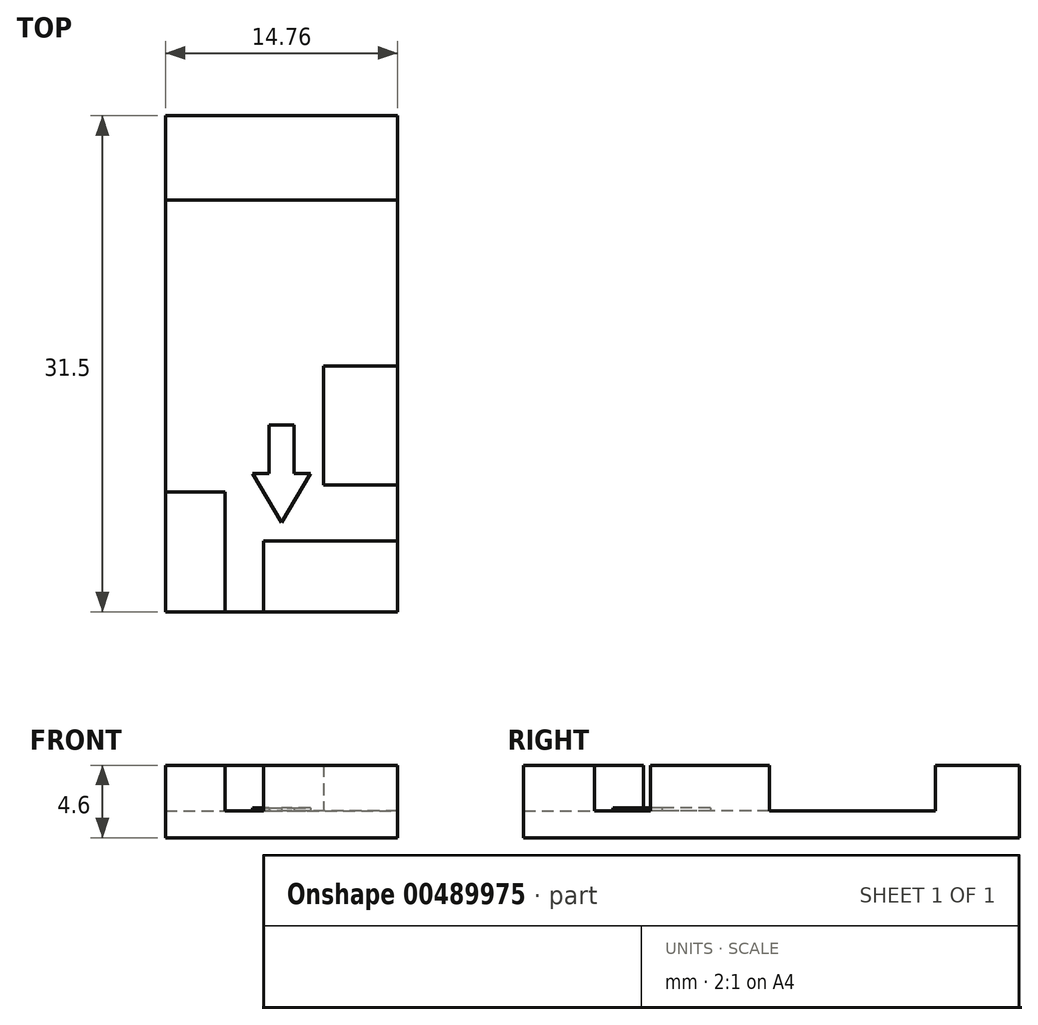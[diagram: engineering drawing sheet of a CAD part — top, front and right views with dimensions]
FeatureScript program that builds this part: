
annotation { "Feature Type Name" : "Feature", "Feature Type Description" : "" }
export const myFeature = defineFeature(function(context is Context, id is Id, definition is map)
    precondition{}
    {
        {
            var Q0;
            Q0=qCreatedBy(makeId("Top.planeOp"),FACE);
            var sketch = newSketch(context, id + "F0", { "sketchPlane" : qUnion([Q0])});
            skLineSegment(sketch, "E0.bottom", {"start": v(7.38, -15.75) * mm, "end": v(-7.38, -15.75) * mm});
            skLineSegment(sketch, "E0.top", {"start": v(7.38, 15.75) * mm, "end": v(-7.37, 15.75) * mm});
            skLineSegment(sketch, "E0.left", {"start": v(7.38, -15.75) * mm, "end": v(7.38, 15.75) * mm});
            skLineSegment(sketch, "E0.right", {"start": v(-7.38, -15.75) * mm, "end": v(-7.37, 15.75) * mm});
            skPoint(sketch, "E0.middle", {"position": v(0, 0) * mm});
            skSolve(sketch);
        }
        {
            var Q0;
            Q0=makeQuery(id+"F0.imprint","IMPRINT",FACE,{"disambiguationData":[TD([[makeQuery(id+"F0.imprint","IMPRINT",EDGE,{"derivedFrom":sQuery(id+"F0.wireOp",EDGE,"E0.bottom")}),-1.0]])]});
            extrude(context, id + "F1", {"entities" : qUnion([Q0]), "depth" : 1.7 * mm});
        }
        {
            var Q0;
            Q0=makeQuery(id+"F1.opExtrude","CAP_FACE",FACE,{"disambiguationData":[OSD([sQuery(id+"F0.wireOp",EDGE,"E0.bottom"),sQuery(id+"F0.wireOp",EDGE,"E0.top"),sQuery(id+"F0.wireOp",EDGE,"E0.left"),sQuery(id+"F0.wireOp",EDGE,"E0.right")])],"isStart":false});
            var sketch = newSketch(context, id + "F2", { "sketchPlane" : qUnion([Q0])});
            skLineSegment(sketch, "E1.bottom", {"start": v(-7.37, 15.75) * mm, "end": v(7.38, 15.75) * mm});
            skLineSegment(sketch, "E1.top", {"start": v(-7.37, 10.4) * mm, "end": v(7.38, 10.4) * mm});
            skLineSegment(sketch, "E1.left", {"start": v(-7.37, 15.75) * mm, "end": v(-7.37, 10.4) * mm});
            skLineSegment(sketch, "E1.right", {"start": v(7.38, 15.75) * mm, "end": v(7.38, 10.4) * mm});
            skLineSegment(sketch, "E2.bottom", {"start": v(7.38, -15.75) * mm, "end": v(-1.12, -15.75) * mm});
            skLineSegment(sketch, "E2.top", {"start": v(7.38, -11.25) * mm, "end": v(-1.13, -11.25) * mm});
            skLineSegment(sketch, "E2.left", {"start": v(7.38, -15.75) * mm, "end": v(7.38, -11.25) * mm});
            skLineSegment(sketch, "E2.right", {"start": v(-1.12, -15.75) * mm, "end": v(-1.13, -11.25) * mm});
            skLineSegment(sketch, "E3.bottom", {"start": v(-7.38, -15.75) * mm, "end": v(-3.57, -15.75) * mm});
            skLineSegment(sketch, "E3.top", {"start": v(-7.38, -8.15) * mm, "end": v(-3.57, -8.15) * mm});
            skLineSegment(sketch, "E3.left", {"start": v(-7.38, -15.75) * mm, "end": v(-7.38, -8.15) * mm});
            skLineSegment(sketch, "E3.right", {"start": v(-3.57, -15.75) * mm, "end": v(-3.57, -8.15) * mm});
            skLineSegment(sketch, "E4.bottom", {"start": v(7.38, -0.15) * mm, "end": v(2.68, -0.15) * mm});
            skLineSegment(sketch, "E4.top", {"start": v(7.38, -7.7) * mm, "end": v(2.68, -7.7) * mm});
            skLineSegment(sketch, "E4.left", {"start": v(7.38, -0.15) * mm, "end": v(7.38, -7.7) * mm});
            skLineSegment(sketch, "E4.right", {"start": v(2.68, -0.15) * mm, "end": v(2.68, -7.7) * mm});
            skSolve(sketch);
        }
        {
            var Q0;
            Q0 = qSketchRegion(id + "F2", true);
            extrude(context, id + "F3", {"entities" : qUnion([Q0]), "operationType" : NewBodyOperationType.ADD, "depth" : 2.9 * mm});
        }
        {
            var Q0;
            Q0=makeQuery(id+"F1.opExtrude","CAP_FACE",FACE,{"disambiguationData":[OSD([sQuery(id+"F0.wireOp",EDGE,"E0.bottom"),sQuery(id+"F0.wireOp",EDGE,"E0.top"),sQuery(id+"F0.wireOp",EDGE,"E0.left"),sQuery(id+"F0.wireOp",EDGE,"E0.right")])],"isStart":false});
            var sketch = newSketch(context, id + "F4", { "sketchPlane" : qUnion([Q0])});
            skLineSegment(sketch, "E5", {"start": v(0, -3.9) * mm, "end": v(0.79, -3.9) * mm});
            skLineSegment(sketch, "E6", {"start": v(0.79, -3.9) * mm, "end": v(0.79, -6.96) * mm});
            skLineSegment(sketch, "E7", {"start": v(0.79, -6.96) * mm, "end": v(1.83, -6.96) * mm});
            skLineSegment(sketch, "E8", {"start": v(1.83, -6.96) * mm, "end": v(0, -10.08) * mm});
            skLineSegment(sketch, "E9.MirrorCS", {"start": v(0, -3.9) * mm, "end": v(-0.79, -3.9) * mm});
            skLineSegment(sketch, "E10.MirrorCS", {"start": v(-0.79, -3.9) * mm, "end": v(-0.79, -6.96) * mm});
            skLineSegment(sketch, "E11.MirrorCS", {"start": v(-0.79, -6.96) * mm, "end": v(-1.83, -6.96) * mm});
            skLineSegment(sketch, "E12.MirrorCS", {"start": v(-1.83, -6.96) * mm, "end": v(0, -10.08) * mm});
            skSolve(sketch);
        }
        {
            var Q0;
            Q0 = qSketchRegion(id + "F4", true);
            extrude(context, id + "F5", {"entities" : qUnion([Q0]), "operationType" : NewBodyOperationType.ADD, "depth" : .2 * mm});
        }
    });
